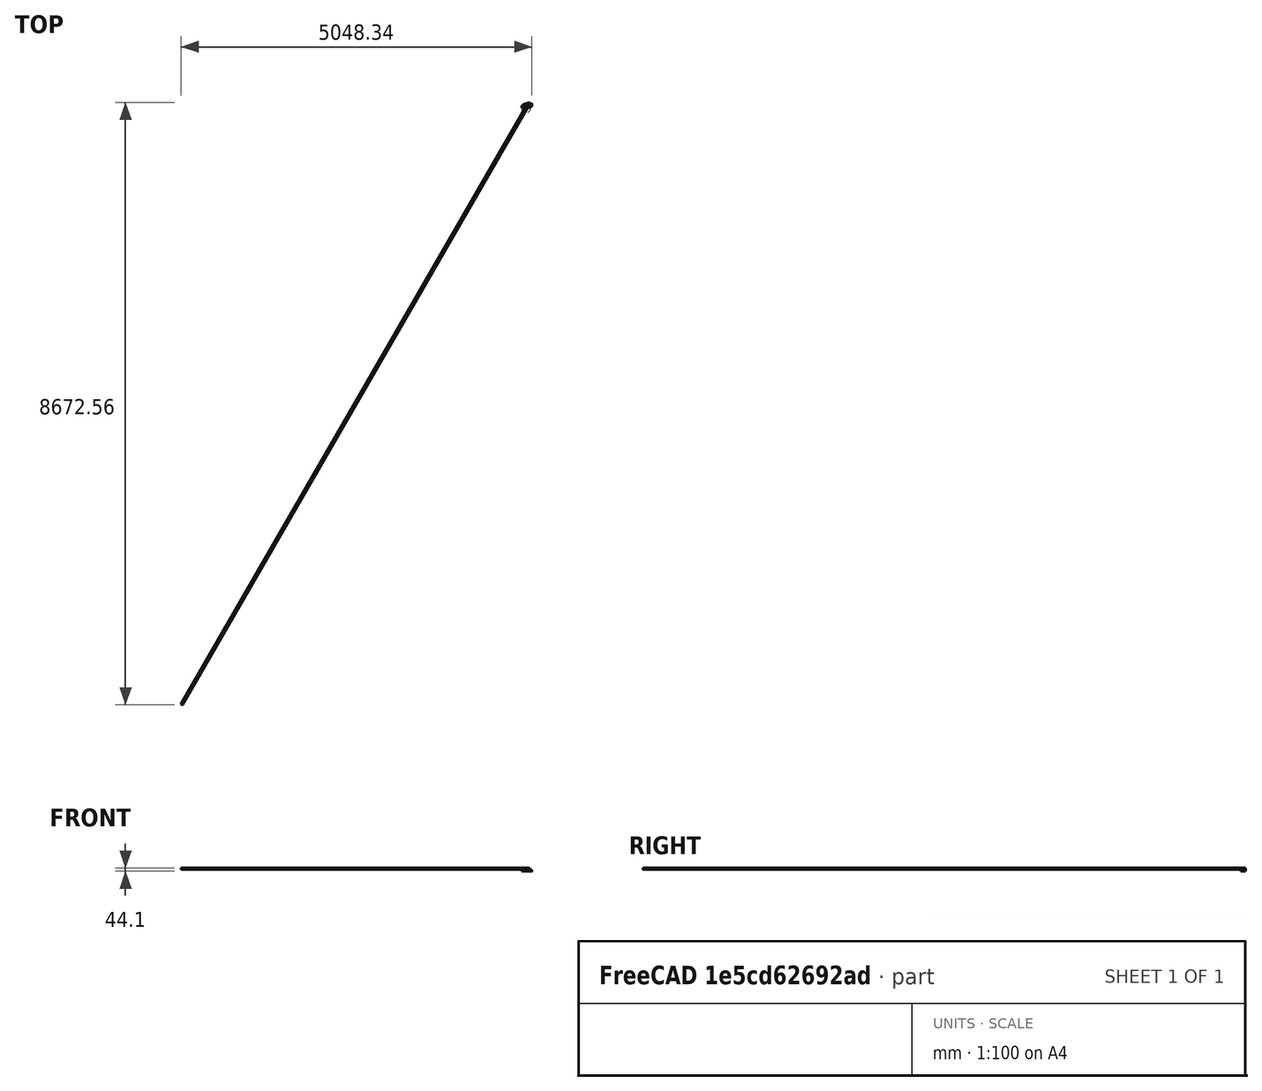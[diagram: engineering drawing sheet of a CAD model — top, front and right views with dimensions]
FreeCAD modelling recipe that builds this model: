
FCSTD DOCUMENT  (FreeCAD 0.16R)
Label: V2
License: All rights reserved
LicenseURL: http://en.wikipedia.org/wiki/All_rights_reserved
objects: Sketcher::SketchObject×6, PartDesign::Pad×4, PartDesign::Fillet×2, PartDesign::Pocket×1, Mesh::Feature×1
note: 18 computed .brp shape members not serialized (recipe doc carries the construction recipe); baked Part::Feature solids carry a one-line shape summary decoded from their .brp

FEATURE [Sketcher::SketchObject] Sketch
  sketch-geometry (11):
    g0: ArcOfCircle CenterX=0 CenterY=0 CenterZ=0 NormalX=0 NormalY=0 NormalZ=1 Radius=65 StartAngle=1.5708 EndAngle=2.86744
    g1: ArcOfCircle CenterX=0 CenterY=0 CenterZ=0 NormalX=0 NormalY=0 NormalZ=1 Radius=48 StartAngle=0.377003 EndAngle=2.75854
    g2: LineSegment StartX=2.40667e-07 StartY=65 StartZ=0 EndX=79.4942 EndY=65 EndZ=0
    g3: LineSegment StartX=47.168 StartY=15.3736 StartZ=0 EndX=54.9232 EndY=15.3842 EndZ=0
    g4: LineSegment StartX=84.8824 StartY=59.6118 StartZ=0 EndX=84.8824 EndY=45.3841 EndZ=0
    g5: ArcOfCircle CenterX=54.8824 CenterY=45.3841 CenterZ=0 NormalX=0 NormalY=0 NormalZ=1 Radius=30 StartAngle=4.71375 EndAngle=6.28319
    g6: ArcOfCircle CenterX=79.4942 CenterY=59.6118 CenterZ=0 NormalX=0 NormalY=0 NormalZ=1 Radius=5.38817 StartAngle=0 EndAngle=1.5708
    g7: ArcOfCircle CenterX=49.0502 CenterY=20.0058 CenterZ=0 NormalX=0 NormalY=0 NormalZ=1 Radius=5 StartAngle=3.62755 EndAngle=4.32643
    g8: ArcOfCircle CenterX=-60.5912 CenterY=17.3257 CenterZ=0 NormalX=0 NormalY=0 NormalZ=1 Radius=2 StartAngle=3.00536 EndAngle=4.40537
    g9: ArcOfCircle CenterX=-48.9002 CenterY=20.3538 CenterZ=0 NormalX=0 NormalY=0 NormalZ=1 Radius=5 StartAngle=4.8743 EndAngle=5.77943
    g10: LineSegment StartX=-61.1956 StartY=15.4192 StartZ=0 EndX=-48.0942 EndY=15.4192 EndZ=0
  constraints (35):
    c: Radius(g0) = 65
    c: Coincident(g-1,g0)
    c: PointOnObject(g1,g-2)
    c: Coincident(g1,g-1)
    c: Radius(g1) = 48
    c: Horizontal(g2)
    c: Coincident(g0,g2)
    c: Vertical(g4)
    c: Tangent(g4,g5) = 1.5708
    c: Tangent(g3,g5) = -1.5708
    c: Tangent(g4,g6) = 1.5708
    c: Tangent(g2,g6) = 1.5708
    c: Radius(g7) = 5
    c: Radius(g9) = 5
    c: Radius(g8) = 2
    c: Coincident(g3,g7)
    c: Coincident(g1,g7)
    c: Coincident(g10,g9)
    c: Coincident(g1,g9)
    c: Coincident(g10,g8)
    c: Coincident(g0,g8)
    c: Distance(g10) = 13.1014
    c: Distance(g2) = 79.4942
    c: Distance(g3) = 7.75526
    c: Distance(g4) = 14.2277
    c: Radius(g5) = 30
    c: Radius(g6) = 5.38817
    c: DistanceY(g-1,g2) = 65
    c: DistanceY(g3) = 15.3736
    c: DistanceY(g9) = 15.4192
    c: DistanceY(g0) = 17.5973
    c: DistanceY(g1) = 17.9402
    c: DistanceY(g8) = 15.4192
    c: DistanceY(g1) = 17.6705
    c: DistanceX(g8) = -61.1956
FEATURE [Sketcher::SketchObject] Sketch002
  Placement = pos=(0,0,1) rot=(0,0,1;0rad)
  sketch-geometry (8):
    g0: ArcOfCircle CenterX=0 CenterY=0 CenterZ=0 NormalX=0 NormalY=0 NormalZ=1 Radius=48 StartAngle=0.377003 EndAngle=2.75854
    g1: LineSegment StartX=47.0328 StartY=15.3736 StartZ=0 EndX=54.7867 EndY=15.2303 EndZ=0
    g2: ArcOfCircle CenterX=55.341 CenterY=45.2252 CenterZ=0 NormalX=0 NormalY=0 NormalZ=1 Radius=30 StartAngle=4.69391 EndAngle=6.10812
    g3: ArcOfCircle CenterX=49.0887 CenterY=19.9313 CenterZ=0 NormalX=0 NormalY=0 NormalZ=1 Radius=5 StartAngle=3.61079 EndAngle=4.28863
    g4: ArcOfCircle CenterX=-48.9021 CenterY=20.3504 CenterZ=0 NormalX=0 NormalY=0 NormalZ=1 Radius=5 StartAngle=4.91142 EndAngle=5.7802
    g5: ArcOfCircle CenterX=-0.655187 CenterY=1.27485 CenterZ=0 NormalX=0 NormalY=0 NormalZ=1 Radius=51 StartAngle=0.862262 EndAngle=2.75615
    g6: LineSegment StartX=84.8825 StartY=40 StartZ=0 EndX=32.5316 EndY=40 EndZ=0
    g7: LineSegment StartX=-47.9135 StartY=20.4491 StartZ=0 EndX=-47.9135 EndY=15.4491 EndZ=0
  constraints (29):
    c: PointOnObject(g0,g-2)
    c: Coincident(g0,g-1)
    c: Radius(g0) = 48
    c: Tangent(g1,g2) = -1.5708
    c: Radius(g3) = 5
    c: Radius(g4) = 5
    c: Coincident(g1,g3)
    c: Coincident(g0,g3)
    c: Coincident(g0,g4)
    c: Distance(g1) = 7.75526
    c: Radius(g2) = 30
    c: DistanceY(g1) = 15.3736
    c: DistanceY(g0) = 17.9402
    c: DistanceY(g0) = 17.6705
    c: DistanceX(g4,g5) = 0
    c: DistanceX(g5) = -47.9135
    c: DistanceY(g4) = 15.4491
    c: DistanceY(g4,g5) = 5
    c: Radius(g5) = 51
    c: Coincident(g6,g2)
    c: Coincident(g5,g6)
    c: Vertical(g7)
    c: Coincident(g7,g5)
    c: Coincident(g7,g4)
    c: DistanceY(g5) = 40
    c: DistanceX(g2) = 84.8825
    c: DistanceY(g1) = 15.2303
    c: DistanceX(g5) = 32.5316
    c: Horizontal(g6)
FEATURE [PartDesign::Pad] Pad002  label="Stiffener"
  Length = 1
  Length2 = 100
  Placement = pos=(0,0,1) rot=(0,0,1;0rad)
  Sketch = -> Sketch002
  Type = 0
FEATURE [PartDesign::Pad] Pad  label="Faceplate"
  Length = 1
  Length2 = 100
  Sketch = -> Sketch
  Type = 0
FEATURE [Sketcher::SketchObject] Sketch001
  Placement = pos=(0,0,1) rot=(0,0,1;0rad)
  Support = -> Pad [Face13]
  sketch-geometry (6):
    g0: ArcOfCircle CenterX=0 CenterY=0 CenterZ=0 NormalX=0 NormalY=0 NormalZ=1 Radius=65 StartAngle=1.5708 EndAngle=2.88461
    g1: LineSegment StartX=6.04881e-05 StartY=65 StartZ=0 EndX=80.0001 EndY=65 EndZ=0
    g2: LineSegment StartX=80.0001 StartY=63 StartZ=0 EndX=6.04881e-05 EndY=63 EndZ=0
    g3: LineSegment StartX=80.0001 StartY=65 StartZ=0 EndX=80.0001 EndY=63 EndZ=0
    g4: ArcOfCircle CenterX=0.26057 CenterY=1.00055 CenterZ=0 NormalX=0 NormalY=0 NormalZ=1 Radius=62 StartAngle=1.575 EndAngle=2.88858
    g5: LineSegment StartX=-62.8655 StartY=16.5204 StartZ=0 EndX=-59.7655 EndY=16.5204 EndZ=0
  constraints (19):
    c: Radius(g0) = 65
    c: Coincident(g-1,g0)
    c: Horizontal(g1)
    c: Coincident(g0,g1)
    c: DistanceY(g-1,g1) = 65
    c: Horizontal(g2)
    c: Equal(g2,g1)
    c: DistanceX(g0,g2) = 0
    c: Coincident(g3,g2)
    c: Coincident(g3,g1)
    c: DistanceY(g2,g1) = 2
    c: Radius(g4) = 62
    c: Coincident(g4,g2)
    c: DistanceX(g0,g4) = 3.1
    c: DistanceY(g4,g0) = 0
    c: DistanceY(g-1,g0) = 16.5204
    c: Coincident(g4,g5)
    c: Coincident(g5,g0)
    c: Distance(g1) = 80
FEATURE [PartDesign::Pad] Pad004  label="Connector"
  Length = 20
  Length2 = 100
  Sketch = -> Sketch001
  Type = 0
FEATURE [PartDesign::Fillet] Fillet
  Base = -> Pad004 [Edge52]
  Radius = 10
FEATURE [PartDesign::Fillet] Fillet001
  Base = -> Fillet [Edge25]
  Radius = 2
FEATURE [Sketcher::SketchObject] Sketch003
  Placement = pos=(0,0,1) rot=(0,0,1;0rad)
  Support = -> Fillet001 [Face14]
FEATURE [Sketcher::SketchObject] Sketch004
  ExternalGeometry = -> [Fillet001]
  Placement = pos=(0,0,1) rot=(0,0,1;0rad)
  Support = -> Fillet001 [Face14]
  sketch-geometry (5):
    g0: LineSegment [constr] StartX=0 StartY=0 StartZ=0 EndX=50 EndY=86.6025 EndZ=0
    g1: LineSegment StartX=31.8675 StartY=85.1962 StartZ=0 EndX=57.8483 EndY=70.1962 EndZ=0
    g2: LineSegment StartX=57.8483 StartY=70.1962 StartZ=0 EndX=54.8483 EndY=65 EndZ=0
    g3: LineSegment StartX=54.8483 StartY=65 StartZ=0 EndX=20.2073 EndY=65 EndZ=0
    g4: LineSegment StartX=20.2073 StartY=65 StartZ=0 EndX=31.8675 EndY=85.1962 EndZ=0
  constraints (15):
    c: Coincident(g0,g-1)
    c: Coincident(g1,g2)
    c: Coincident(g2,g3)
    c: Coincident(g3,g4)
    c: Coincident(g4,g1)
    c: Perpendicular(g0,g1)
    c: Parallel(g4,g0)
    c: Parallel(g2,g0)
    c: Distance(g1) = 30
    c: Symmetric(g1,g1,g0)
    c: Parallel(g3,g-3)
    c: Distance(g2) = 6
    c: PointOnObject(g3,g-3)
    c: Angle(g0) = 1.0472
    c: Distance(g0) = 100
FEATURE [PartDesign::Pad] Pad005
  Length = 34.5
  Length2 = 1
  Sketch = -> Sketch004
  Type = 4
FEATURE [Sketcher::SketchObject] Sketch005
  Placement = pos=(44.8579,77.6962,0) rot=(0.186157,0.694747,0.694747;2.77349rad)
  Support = -> Pad005 [Face1]
  sketch-geometry (1):
    g0: Circle CenterX=0 CenterY=34.5 CenterZ=0 NormalX=0 NormalY=0 NormalZ=1 Radius=9.6
  constraints (3):
    c: PointOnObject(g0,g-2)
    c: Radius(g0) = 9.6
    c: DistanceY(g-1,g0) = 34.5
FEATURE [PartDesign::Pocket] Pocket
  Length = 5
  Sketch = -> Sketch005
  Type = 1
FEATURE [Mesh::Feature] Mesh  label="Pocket (Meshed)"
